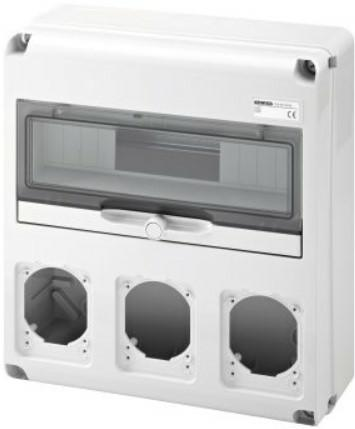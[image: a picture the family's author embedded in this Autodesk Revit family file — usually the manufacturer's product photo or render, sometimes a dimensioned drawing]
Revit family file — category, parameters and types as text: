
# Revit family: Building-IEC309Boards-GEWISS-68QDIN-DISTRIBUTION-BOARD-14MOD_3SOCKET-OUTLETS
name_source: partatom
category: Apparecchi elettrici
units: mm (PartAtom-declared; Revit-internal decimal feet)

## family parameters
Condiviso = No
Host = Superficie
Mantenere orientamento annotazione = Sì
Punto di calcolo locali = Sì
Quota connettore circolare = Usa diametro
Taglio con vuoti quando caricato = No
Tipo di parte = Normale

## types (1)
- GW68005N - Q-DIN 14M 3 FLANGES S.O.16/32A IP65
    Accordance with Standards = EN 60208 - EN 60670-1 - IEC 60670-24
    Catalogue = BUILDING
    Catalogue Range = 68 QDIN
    Colour = Grey RAL 7035
    Descrizione = Q-DIN 14M 3 FLANGES S.O.16/32A IP65
    Dispersible power A (W) = 24
    Dispersible power B (W) = 64
    EAN code = 8011564744769
    Electrocod = 2242
    Glow Wire Test = 650°C
    Houseable socket = 3 IEC 309 16/32A IP44/67
    IDF = 195ebcb1-dd8e-40fd-99da-a97f76e872ef
    IDT = 63e6b50c-c9b0-4c82-844b-021dcb4b6831
    IP degree = IP65
    Immagine tipo = GW68005N.jpg
    Installation type = Surface-mounting
    Insulation class = II
    Modello = GW68005N
    No. of blank lids supplied = 1 IB 16/32A
    No. of modules EN 50022 = 14
    No. of provided blank lids = 1 IEC 16/32A
    Operating temperature: = -25 +40 °C
    POMELLO = bianco
    PRESA = rosso
    Produttore = GEWISS S.p.A.
    Prospetto di default = 1219 mm
    SEO = Board
    STRUTTURA = RAL - 7035
    STRUTTURA ALTA = Poche
    Shock resistance = IK08
    Spostamento_S = 1000 mm  [stored 3.28084 ft]
    Technical sheet = https://www.gewiss.com
    Thermo-pressure with ball = 70
    URL = https://www.gewiss.com
    VETRO = Vetro
    Version file RFA = 21.5
    Version type = Empty
    Working temperature = -25 ÷ +40 °C

note: source unit labels omitted for Thermo-pressure with ball — the stored unit's dimension contradicts the parameter name (converter mislabeling)

note: [stored X ft] marks values corroborated as IEEE doubles in the binary element streams (Revit-internal decimal feet)

## geometry (parser evidence)
native form markers: Sweep x4
no freeform markers — native parametric forms only
